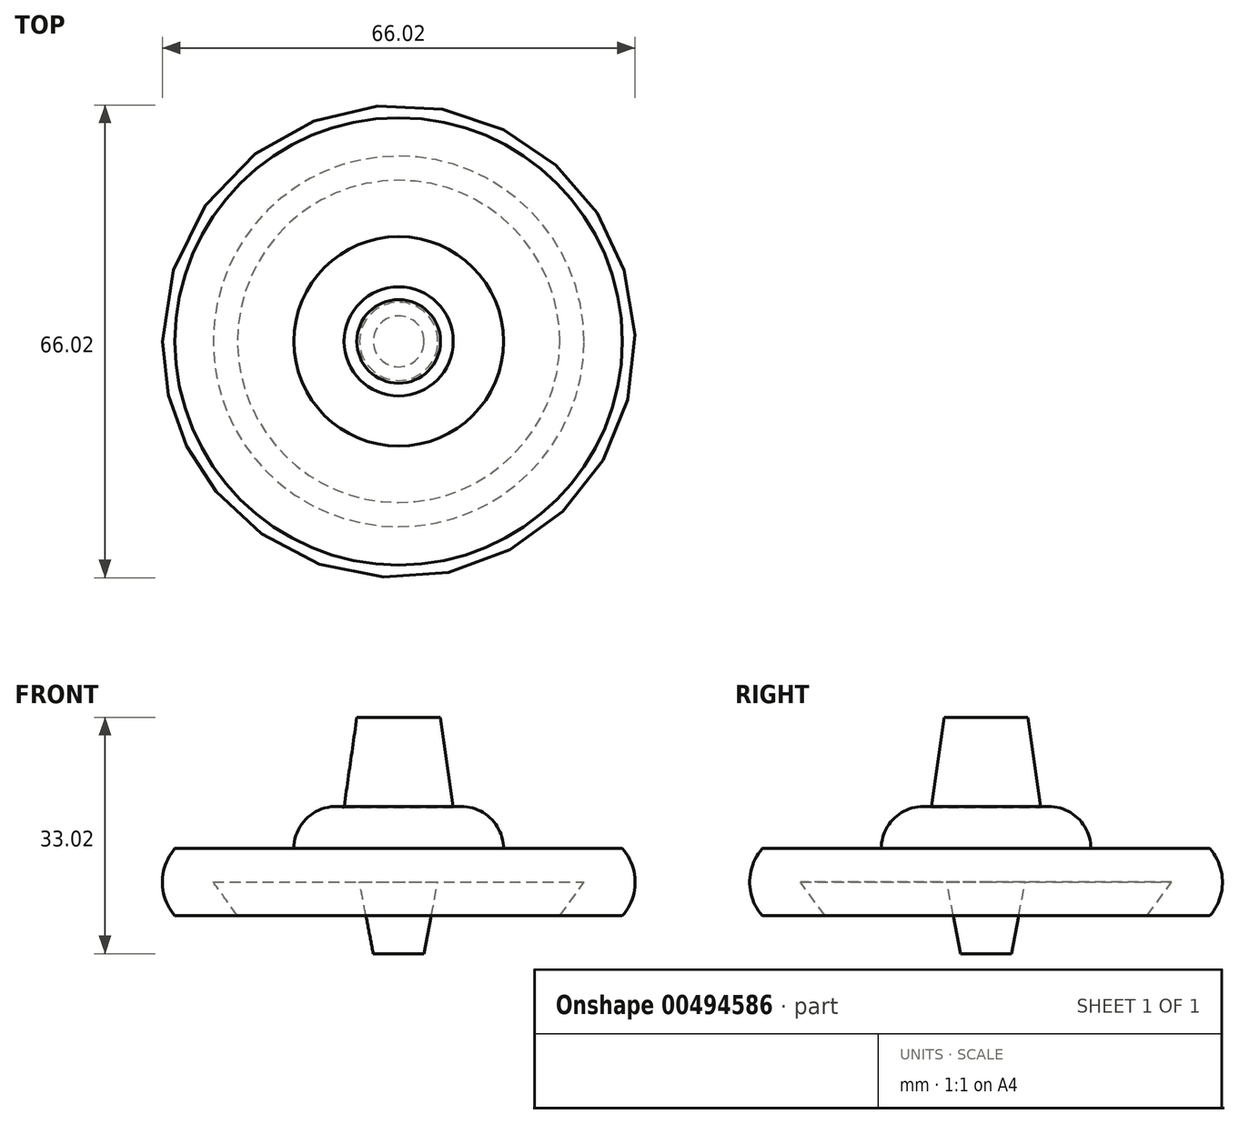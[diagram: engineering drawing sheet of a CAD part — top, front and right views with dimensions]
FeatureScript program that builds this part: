
annotation { "Feature Type Name" : "Feature", "Feature Type Description" : "" }
export const myFeature = defineFeature(function(context is Context, id is Id, definition is map)
    precondition{}
    {
        {
            var Q0;
            Q0=qCreatedBy(makeId("Front.planeOp"),FACE);
            var sketch = newSketch(context, id + "F0", { "sketchPlane" : qUnion([Q0])});
            skLineSegment(sketch, "E0", {"start": v(0, 31.23) * mm, "end": v(5.84, 31.23) * mm});
            skLineSegment(sketch, "E1", {"start": v(5.84, 31.23) * mm, "end": v(7.62, 18.66) * mm});
            skArc(sketch, "E2", {"start": v(14.64, 12.9) * mm, "mid": v(12.49, 17.43) * mm, "end": v(7.62, 18.66) * mm});
            skLineSegment(sketch, "E3", {"start": v(14.64, 12.9) * mm, "end": v(31.24, 12.9) * mm});
            skArc(sketch, "E4", {"start": v(31.24, 3.5) * mm, "mid": v(33.01, 8.2) * mm, "end": v(31.24, 12.9) * mm});
            skLineSegment(sketch, "E5", {"start": v(31.24, 3.5) * mm, "end": v(22.5, 3.5) * mm});
            skLineSegment(sketch, "E6", {"start": v(22.5, 3.5) * mm, "end": v(25.89, 8.2) * mm});
            skLineSegment(sketch, "E7", {"start": v(25.89, 8.2) * mm, "end": v(5.46, 8.2) * mm});
            skLineSegment(sketch, "E8", {"start": v(5.46, 8.2) * mm, "end": v(3.55, -1.79) * mm});
            skLineSegment(sketch, "E9", {"start": v(3.55, -1.79) * mm, "end": v(0, -1.79) * mm});
            skLineSegment(sketch, "E10", {"start": v(0, -1.79) * mm, "end": v(0, 31.23) * mm});
            skSolve(sketch);
        }
        {
            var Q0;
            Q0=makeQuery(id+"F0.imprint","IMPRINT",FACE,{"disambiguationData":[TD([[makeQuery(id+"F0.imprint","IMPRINT",EDGE,{"derivedFrom":sQuery(id+"F0.wireOp",EDGE,"E0")}),-1.0]])]});
            var Q1;
            Q1=sQuery(id+"F0.wireOp",EDGE,"E10");
            revolve(context, id + "F1", {"entities" : qUnion([Q0]), "axis" : qUnion([Q1]), "revolveType" : RevolveType.FULL});
        }
    });
